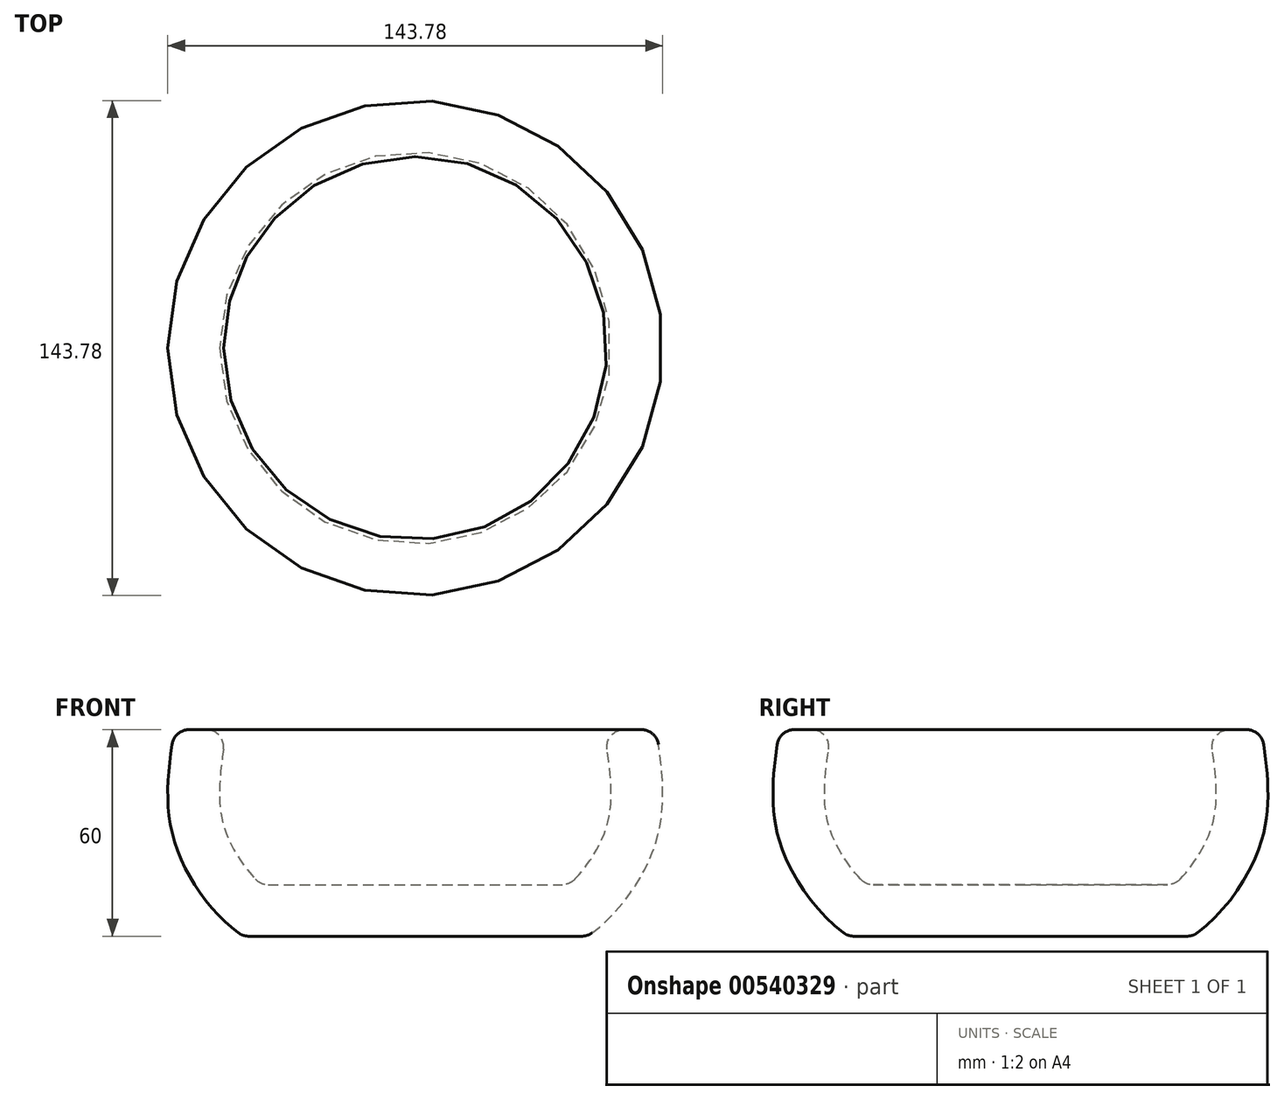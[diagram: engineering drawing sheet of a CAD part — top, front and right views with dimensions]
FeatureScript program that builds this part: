
annotation { "Feature Type Name" : "Feature", "Feature Type Description" : "" }
export const myFeature = defineFeature(function(context is Context, id is Id, definition is map)
    precondition{}
    {
        {
            var Q0;
            Q0=qCreatedBy(makeId("Front.planeOp"),FACE);
            var sketch = newSketch(context, id + "F0", { "sketchPlane" : qUnion([Q0])});
            skLineSegment(sketch, "E0", {"start": v(0, 0) * mm, "end": v(-50, 0) * mm});
            skLineSegment(sketch, "E1", {"start": v(0, 60) * mm, "end": v(-70, 60) * mm});
            skFitSpline(sketch, "E2", {"points": [v(-70, 60) * mm, v(-70, 27.65) * mm, v(-50, 0) * mm], "startDerivative": vector(-10.77, -68.09) * mm, "endDerivative": vector(51.48, -34.95) * mm});
            skLineSegment(sketch, "E3", {"start": v(0, 0) * mm, "end": v(0, 60) * mm});
            skSolve(sketch);
        }
        {
            var Q0;
            Q0=makeQuery(id+"F0.imprint","IMPRINT",FACE,{"disambiguationData":[TD([[makeQuery(id+"F0.imprint","IMPRINT",EDGE,{"derivedFrom":sQuery(id+"F0.wireOp",EDGE,"E0")}),-1.0]])]});
            var Q1;
            Q1=sQuery(id+"F0.wireOp",EDGE,"E3");
            revolve(context, id + "F1", {"entities" : qUnion([Q0]), "axis" : qUnion([Q1]), "revolveType" : RevolveType.FULL});
        }
        {
            var Q0;
            Q0=makeQuery(id+"F1.opRevolve","SWEPT_FACE",FACE,{"disambiguationData":[OSD([sQuery(id+"F0.wireOp",EDGE,"E1")])]});
            shell(context, id + "F2", {"entities" : qUnion([Q0]), "thickness" : 15 * mm});
        }
        {
            var Q0;
            Q0=makeQuery(id+"F1.opRevolve","SWEPT_EDGE",EDGE,{"disambiguationData":[OSD([sQuery(id+"F0.wireOp",EDGE,"E1"),sQuery(id+"F0.wireOp",EDGE,"E2")])]});
            var Q1;
            Q1=makeQuery(id+"F2.opShell","OFFSET_EDGE",EDGE,{"disambiguationData":[OSD([sQuery(id+"F0.wireOp",EDGE,"E1"),sQuery(id+"F0.wireOp",EDGE,"E2")])]});
            var Q2;
            Q2=makeQuery(id+"F2.opShell","OFFSET_FACE",FACE,{"disambiguationData":[OSD([sQuery(id+"F0.wireOp",EDGE,"E0")])]});
            var Q3;
            Q3=makeQuery(id+"F1.opRevolve","SWEPT_EDGE",EDGE,{"disambiguationData":[OSD([sQuery(id+"F0.wireOp",EDGE,"E0"),sQuery(id+"F0.wireOp",EDGE,"E2")])]});
            fillet(context, id + "F3", {"entities" : qUnion([Q0, Q1, Q2, Q3]), "radius" : 5 * mm, "tangentPropagation" : true, "allowEdgeOverflow" : false});
        }
    });
